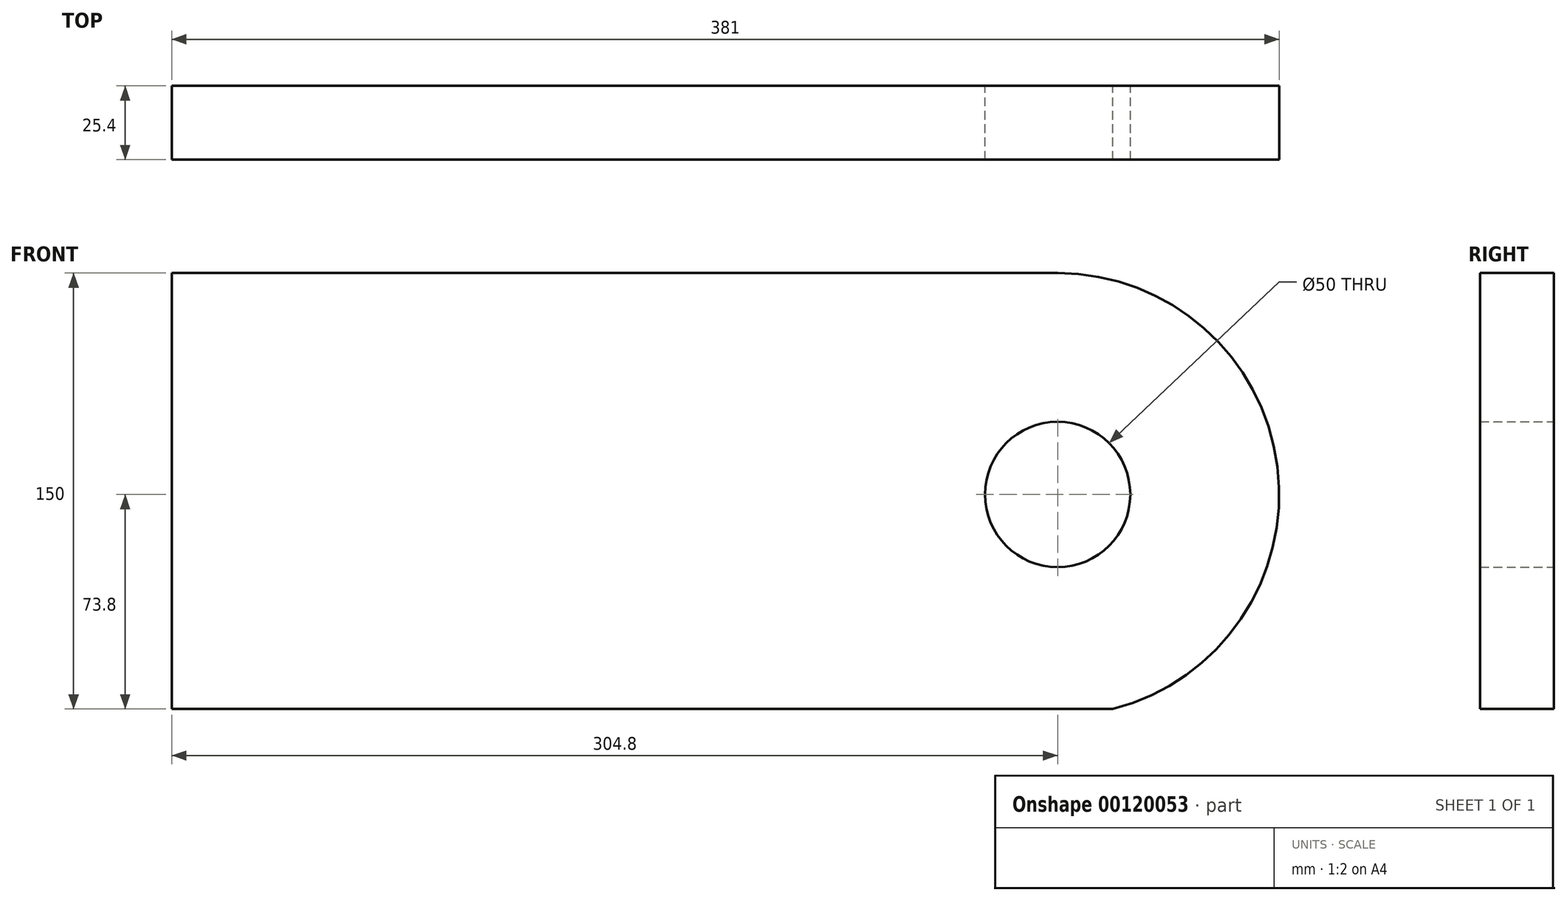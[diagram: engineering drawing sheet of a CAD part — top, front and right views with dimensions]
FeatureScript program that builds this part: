
annotation { "Feature Type Name" : "Feature", "Feature Type Description" : "" }
export const myFeature = defineFeature(function(context is Context, id is Id, definition is map)
    precondition{}
    {
        {
            var Q0;
            Q0=qCreatedBy(makeId("Front.planeOp"),FACE);
            var sketch = newSketch(context, id + "F0", { "sketchPlane" : qUnion([Q0])});
            skLineSegment(sketch, "E0", {"start": v(18.97, 0) * mm, "end": v(-304.8, 0) * mm});
            skLineSegment(sketch, "E1", {"start": v(-304.8, 0) * mm, "end": v(-304.8, 150) * mm});
            skLineSegment(sketch, "E2", {"start": v(-304.8, 150) * mm, "end": v(0, 150) * mm});
            skArc(sketch, "E3", {"start": v(18.97, 0) * mm, "mid": v(75.6, 83.36) * mm, "end": v(0, 150) * mm});
            skCircle(sketch, "E4", {"center": v(0, 73.8) * mm, "radius": 25 * mm});
            skSolve(sketch);
        }
        {
            var Q0;
            Q0 = qSketchRegion(id + "F0", true);
            extrude(context, id + "F1", {"entities" : qUnion([Q0]), "depth" : 25.4 * mm});
        }
    });
